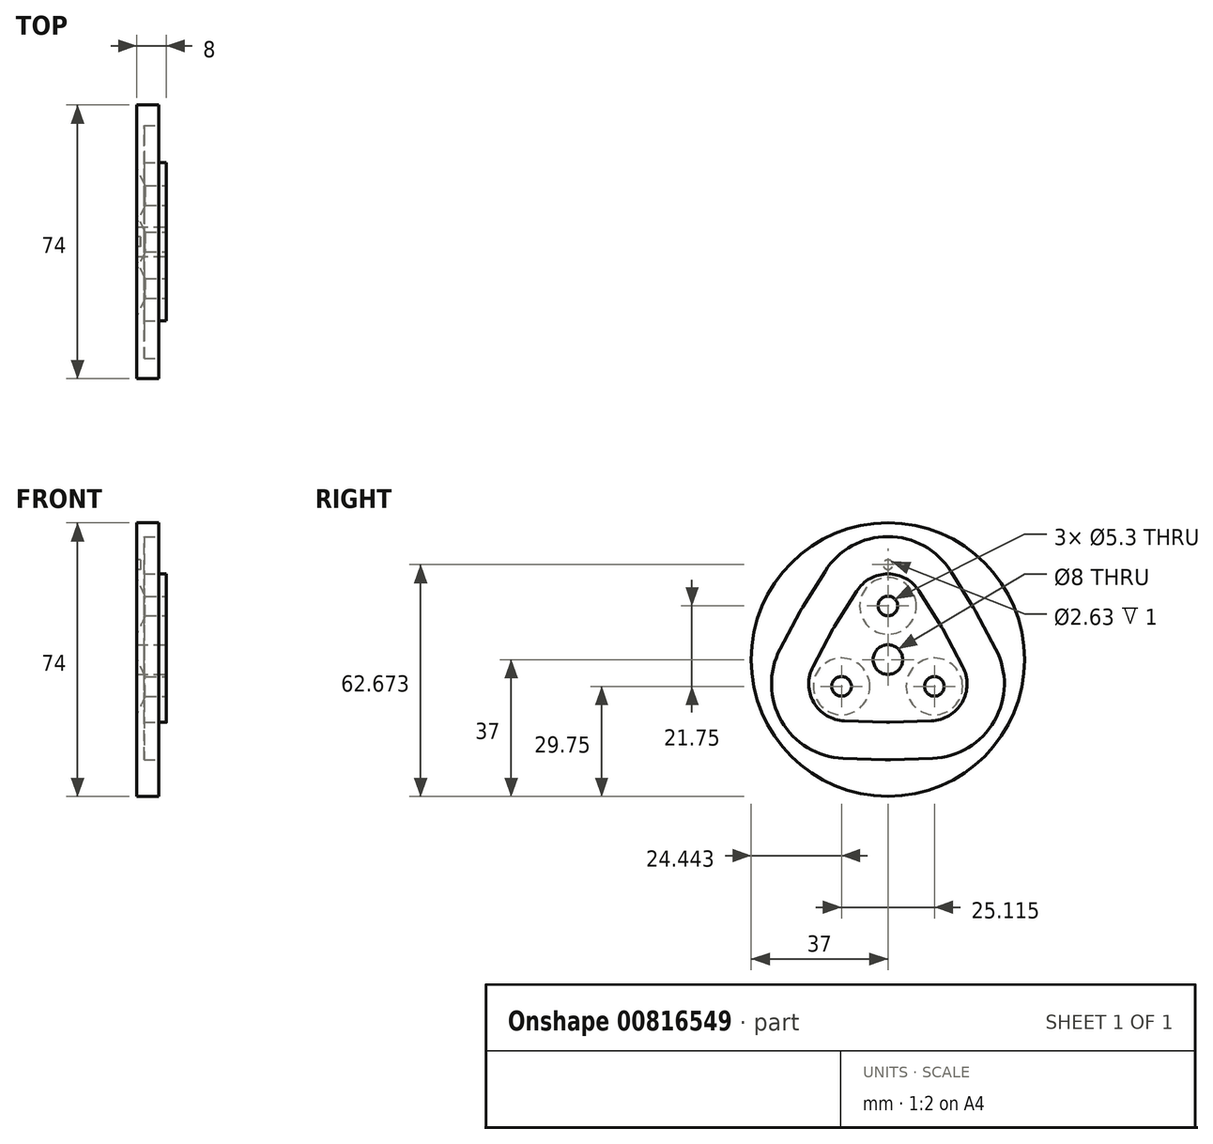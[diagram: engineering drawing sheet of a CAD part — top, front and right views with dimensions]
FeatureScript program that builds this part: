
annotation { "Feature Type Name" : "Feature", "Feature Type Description" : "" }
export const myFeature = defineFeature(function(context is Context, id is Id, definition is map)
    precondition{}
    {
        {
            var Q0;
            Q0=qCreatedBy(makeId("Right.planeOp"),FACE);
            var sketch = newSketch(context, id + "F0", { "sketchPlane" : qUnion([Q0])});
            skCircle(sketch, "E0", {"center": v(0, 0) * mm, "radius": 37 * mm});
            skCircle(sketch, "E1", {"center": v(0, 0) * mm, "radius": 4 * mm});
            skLineSegment(sketch, "E2", {"start": v(0, 50.53) * mm, "end": v(0, -45.3) * mm, "construction": true});
            skLineSegment(sketch, "E3", {"start": v(0, 0) * mm, "end": v(28.08, 48.64) * mm, "construction": true});
            skLineSegment(sketch, "E4", {"start": v(0, 0) * mm, "end": v(48.73, -28.13) * mm, "construction": true});
            skLineSegment(sketch, "E5.MirrorCS", {"start": v(43.76, 25.27) * mm, "end": v(-39.22, -22.65) * mm, "construction": true});
            skLineSegment(sketch, "E6.MirrorCS", {"start": v(0, 0) * mm, "end": v(-28.08, 48.64) * mm, "construction": true});
            skLineSegment(sketch, "E7.MirrorCS", {"start": v(-43.76, 25.27) * mm, "end": v(39.22, -22.65) * mm, "construction": true});
            skLineSegment(sketch, "E8.MirrorCS", {"start": v(0, 0) * mm, "end": v(-28.08, -48.64) * mm, "construction": true});
            skLineSegment(sketch, "E9.MirrorCS", {"start": v(0, 0) * mm, "end": v(28.08, -48.64) * mm, "construction": true});
            skLineSegment(sketch, "E10", {"start": v(-8.48, 18.48) * mm, "end": v(-14.54, 8.81) * mm});
            skLineSegment(sketch, "E11", {"start": v(-14.9, 8.18) * mm, "end": v(-20.25, -1.9) * mm});
            skLineSegment(sketch, "E12", {"start": v(-11.78, -16.58) * mm, "end": v(-0.36, -17) * mm});
            skLineSegment(sketch, "E13", {"start": v(0.36, -17) * mm, "end": v(11.77, -16.58) * mm});
            skLineSegment(sketch, "E14", {"start": v(20.24, -1.9) * mm, "end": v(14.9, 8.18) * mm});
            skLineSegment(sketch, "E15", {"start": v(14.53, 8.8) * mm, "end": v(8.47, 18.48) * mm});
            skPoint(sketch, "E16.visualSharp", {"position": v(0, 32) * mm});
            skArc(sketch, "E16.filletArc", {"start": v(8.47, 18.48) * mm, "mid": v(0, 23.17) * mm, "end": v(-8.48, 18.48) * mm});
            skPoint(sketch, "E17.visualSharp", {"position": v(-14.73, 8.5) * mm});
            skArc(sketch, "E17.filletArc", {"start": v(-14.54, 8.81) * mm, "mid": v(-14.73, 8.5) * mm, "end": v(-14.9, 8.18) * mm});
            skPoint(sketch, "E18.visualSharp", {"position": v(-27.71, -16) * mm});
            skArc(sketch, "E18.filletArc", {"start": v(-20.25, -1.9) * mm, "mid": v(-20.07, -11.59) * mm, "end": v(-11.78, -16.58) * mm});
            skPoint(sketch, "E19.visualSharp", {"position": v(0, -17.01) * mm});
            skArc(sketch, "E19.filletArc", {"start": v(-0.36, -17) * mm, "mid": v(0, -17) * mm, "end": v(0.36, -17) * mm});
            skPoint(sketch, "E20.visualSharp", {"position": v(27.71, -16) * mm});
            skArc(sketch, "E20.filletArc", {"start": v(11.77, -16.58) * mm, "mid": v(20.07, -11.59) * mm, "end": v(20.24, -1.9) * mm});
            skPoint(sketch, "E21.visualSharp", {"position": v(14.72, 8.5) * mm});
            skArc(sketch, "E21.filletArc", {"start": v(14.9, 8.18) * mm, "mid": v(14.72, 8.5) * mm, "end": v(14.53, 8.8) * mm});
            skLineSegment(sketch, "E22.0", {"start": v(-17.03, 23.85) * mm, "end": v(-23.1, 14.18) * mm});
            skArc(sketch, "E22.1", {"start": v(-0.73, -27.1) * mm, "mid": v(0, -27.1) * mm, "end": v(0.73, -27.1) * mm});
            skLineSegment(sketch, "E22.2", {"start": v(-12.14, -26.67) * mm, "end": v(-0.73, -27.1) * mm});
            skArc(sketch, "E22.3", {"start": v(-29.17, 2.82) * mm, "mid": v(-28.82, -16.64) * mm, "end": v(-12.14, -26.67) * mm});
            skLineSegment(sketch, "E22.4", {"start": v(-23.83, 12.91) * mm, "end": v(-29.17, 2.82) * mm});
            skLineSegment(sketch, "E22.5", {"start": v(0.73, -27.1) * mm, "end": v(12.14, -26.68) * mm});
            skArc(sketch, "E22.6", {"start": v(-23.1, 14.18) * mm, "mid": v(-23.47, 13.55) * mm, "end": v(-23.83, 12.91) * mm});
            skArc(sketch, "E22.7", {"start": v(12.14, -26.68) * mm, "mid": v(28.81, -16.63) * mm, "end": v(29.16, 2.83) * mm});
            skLineSegment(sketch, "E22.8", {"start": v(29.16, 2.83) * mm, "end": v(23.81, 12.91) * mm});
            skArc(sketch, "E22.9", {"start": v(23.81, 12.91) * mm, "mid": v(23.46, 13.55) * mm, "end": v(23.09, 14.17) * mm});
            skLineSegment(sketch, "E22.10", {"start": v(23.09, 14.17) * mm, "end": v(17.03, 23.84) * mm});
            skArc(sketch, "E22.11", {"start": v(17.03, 23.84) * mm, "mid": v(0, 33.27) * mm, "end": v(-17.03, 23.85) * mm});
            skCircle(sketch, "E23", {"center": v(0, 0) * mm, "radius": 14.5 * mm, "construction": true});
            skCircle(sketch, "E24", {"center": v(-12.56, -7.25) * mm, "radius": 2.65 * mm});
            skCircle(sketch, "E25", {"center": v(12.56, -7.25) * mm, "radius": 2.65 * mm});
            skCircle(sketch, "E26", {"center": v(0, 14.5) * mm, "radius": 2.65 * mm});
            skSolve(sketch);
        }
        {
            var Q0;
            Q0=qSketchRegion(id+"F0",true);
            var Q1;
            Q1=makeQuery(id+"F0.imprint","IMPRINT",FACE,{"disambiguationData":[TD([[makeQuery(id+"F0.imprint","IMPRINT",EDGE,{"derivedFrom":sQuery(id+"F0.wireOp",EDGE,"E10")}),-1.0]])]});
            var Q2;
            Q2=makeQuery(id+"F0.imprint","IMPRINT",FACE,{"disambiguationData":[TD([[makeQuery(id+"F0.imprint","IMPRINT",EDGE,{"derivedFrom":sQuery(id+"F0.wireOp",EDGE,"E1")}),-1.0]])]});
            extrude(context, id + "F1", {"entities" : qUnion([Q0, Q1, Q2]), "oppositeDirection" : true, "depth" : 6 * mm, "offsetDistance" : 25 * mm});
        }
        {
            var Q0;
            Q0=makeQuery(id+"F0.imprint","IMPRINT",FACE,{"disambiguationData":[TD([[makeQuery(id+"F0.imprint","IMPRINT",EDGE,{"derivedFrom":sQuery(id+"F0.wireOp",EDGE,"E10")}),-1.0]])]});
            extrude(context, id + "F2", {"entities" : qUnion([Q0]), "operationType" : NewBodyOperationType.REMOVE, "oppositeDirection" : true, "depth" : 4 * mm, "offsetDistance" : 25 * mm});
        }
        {
            var Q0;
            {var subQ0=sQuery(id+"F0.wireOp",EDGE,"E1");Q0=makeQuery(id+"F2.boolean.opBoolean","SPLIT",FACE,{"disambiguationData":[TD([makeQuery(id+"F1.opExtrude","SWEPT_FACE",FACE,{"disambiguationData":[OSD([subQ0])]})])],"derivedFrom":makeQuery(id+"F1.opExtrude","CAP_FACE",FACE,{"disambiguationData":[OSD([sQuery(id+"F0.wireOp",EDGE,"E0"),subQ0])],"isStart":true})});}
            extrude(context, id + "F3", {"entities" : qUnion([Q0]), "operationType" : NewBodyOperationType.ADD, "depth" : 2 * mm, "offsetDistance" : 25 * mm});
        }
        {
            var Q0;
            Q0=makeQuery(id+"F1.opExtrude","CAP_EDGE",EDGE,{"disambiguationData":[OSD([sQuery(id+"F0.wireOp",EDGE,"E26")])],"isStart":false});
            var Q1;
            Q1=makeQuery(id+"F1.opExtrude","CAP_EDGE",EDGE,{"disambiguationData":[OSD([sQuery(id+"F0.wireOp",EDGE,"E25")])],"isStart":false});
            var Q2;
            Q2=makeQuery(id+"F1.opExtrude","CAP_EDGE",EDGE,{"disambiguationData":[OSD([sQuery(id+"F0.wireOp",EDGE,"E24")])],"isStart":false});
            chamfer(context, id + "F4", {"entities" : qUnion([Q0, Q1, Q2]), "chamferType" : ChamferType.TWO_OFFSETS, "width1" : 5 * mm, "oppositeDirection" : false, "width2" : 2.3 * mm, "tangentPropagation" : true});
        }
        {
            var Q0;
            Q0=makeQuery(id+"F1.opExtrude","CAP_FACE",FACE,{"disambiguationData":[OSD([sQuery(id+"F0.wireOp",EDGE,"E0"),sQuery(id+"F0.wireOp",EDGE,"E1"),sQuery(id+"F0.wireOp",EDGE,"E24"),sQuery(id+"F0.wireOp",EDGE,"E25"),sQuery(id+"F0.wireOp",EDGE,"E26")])],"isStart":false});
            var sketch = newSketch(context, id + "F5", { "sketchPlane" : qUnion([Q0])});
            skLineSegment(sketch, "E27", {"start": v(-34.41, 25.67) * mm, "end": v(51.35, 25.67) * mm, "construction": true});
            skCircle(sketch, "E28", {"center": v(0, 0) * mm, "radius": 25.67 * mm, "construction": true});
            skCircle(sketch, "E29", {"center": v(0, 25.67) * mm, "radius": 1.31 * mm});
            skSolve(sketch);
        }
        {
            var Q0;
            Q0=makeQuery(id+"F5.imprint","IMPRINT",FACE,{"disambiguationData":[TD([[makeQuery(id+"F5.imprint","IMPRINT",EDGE,{"derivedFrom":sQuery(id+"F5.wireOp",EDGE,"E29")}),1.0]])]});
            var Q1;
            Q1=sQuery(id+"F5.wireOp",EDGE,"E29");
            extrude(context, id + "F6", {"entities" : qUnion([Q0]), "operationType" : NewBodyOperationType.REMOVE, "surfaceEntities" : qUnion([Q1]), "oppositeDirection" : true, "depth" : 1 * mm, "offsetDistance" : 25 * mm});
        }
    });
